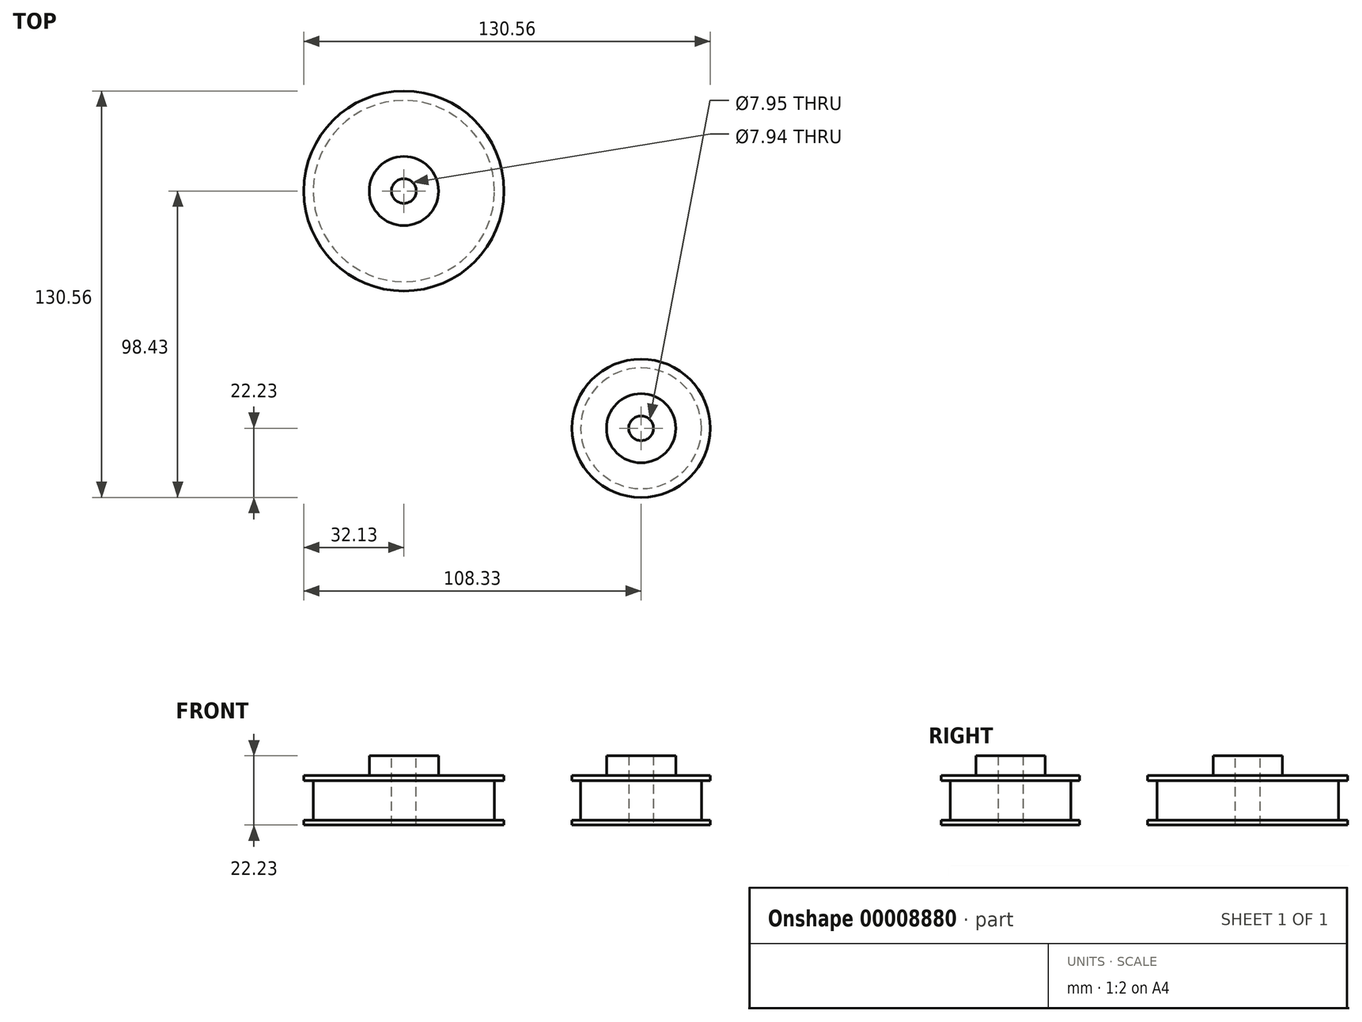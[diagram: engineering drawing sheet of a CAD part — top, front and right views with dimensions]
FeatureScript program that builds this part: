
annotation { "Feature Type Name" : "Feature", "Feature Type Description" : "" }
export const myFeature = defineFeature(function(context is Context, id is Id, definition is map)
    precondition{}
    {
        {
            var Q0;
            Q0=qCreatedBy(makeId("Front.planeOp"),FACE);
            var sketch = newSketch(context, id + "F0", { "sketchPlane" : qUnion([Q0])});
            skLineSegment(sketch, "E0", {"start": v(-11.11, 22.23) * mm, "end": v(11.11, 22.23) * mm});
            skLineSegment(sketch, "E1", {"start": v(11.11, 22.23) * mm, "end": v(11.11, 15.87) * mm});
            skLineSegment(sketch, "E2", {"start": v(11.11, 15.87) * mm, "end": v(32.13, 15.88) * mm});
            skLineSegment(sketch, "E3", {"start": v(32.13, 15.87) * mm, "end": v(32.13, 14.29) * mm});
            skLineSegment(sketch, "E4", {"start": v(32.13, 14.29) * mm, "end": v(29.1, 14.29) * mm});
            skLineSegment(sketch, "E5", {"start": v(29.1, 14.29) * mm, "end": v(29.1, 1.59) * mm});
            skLineSegment(sketch, "E6", {"start": v(29.1, 1.59) * mm, "end": v(32.13, 1.59) * mm});
            skLineSegment(sketch, "E7", {"start": v(32.13, 1.59) * mm, "end": v(32.13, 0) * mm});
            skLineSegment(sketch, "E8", {"start": v(32.13, 0) * mm, "end": v(-32.13, 0) * mm});
            skLineSegment(sketch, "E9", {"start": v(-32.13, 0) * mm, "end": v(-32.13, 1.59) * mm});
            skLineSegment(sketch, "E10", {"start": v(-32.13, 1.59) * mm, "end": v(-29.1, 1.59) * mm});
            skLineSegment(sketch, "E11", {"start": v(-29.1, 1.59) * mm, "end": v(-29.1, 14.29) * mm});
            skLineSegment(sketch, "E12", {"start": v(-29.1, 14.29) * mm, "end": v(-32.13, 14.29) * mm});
            skLineSegment(sketch, "E13", {"start": v(-32.13, 14.29) * mm, "end": v(-32.13, 15.87) * mm});
            skLineSegment(sketch, "E14", {"start": v(-32.13, 15.87) * mm, "end": v(-11.11, 15.87) * mm});
            skLineSegment(sketch, "E15", {"start": v(-11.11, 15.87) * mm, "end": v(-11.11, 22.23) * mm});
            skLineSegment(sketch, "E16", {"start": v(0, 22.23) * mm, "end": v(0, 0) * mm, "construction": true});
            skLineSegment(sketch, "E17", {"start": v(-3.97, 22.23) * mm, "end": v(-3.97, 0) * mm});
            skLineSegment(sketch, "E18", {"start": v(3.97, 22.23) * mm, "end": v(3.97, 0) * mm});
            skSolve(sketch);
        }
        {
            var Q0;
            {var subQ3=sQuery(id+"F0.wireOp",EDGE,"E1");Q0=makeQuery(id+"F0.imprint","IMPRINT",FACE,{"disambiguationData":[TD([[makeQuery(id+"F0.imprint","IMPRINT",EDGE,{"derivedFrom":subQ3}),-1.0]])]});}
            var Q1;
            Q1=sQuery(id+"F0.wireOp",EDGE,"E16");
            revolve(context, id + "F1", {"entities" : qUnion([Q0]), "axis" : qUnion([Q1]), "revolveType" : RevolveType.FULL});
        }
        {
            var Q0;
            Q0=qCreatedBy(makeId("Front.planeOp"),FACE);
            cPlane(context, id + "F2", {"entities" : qUnion([Q0]), "cplaneType" : CPlaneType.OFFSET, "offset" : 76.2 * mm, "width" : 152.4 * mm, "height" : 152.4 * mm});
        }
        {
            var Q0;
            Q0=qCreatedBy(id+"F2.planeOp",FACE);
            var sketch = newSketch(context, id + "F3", { "sketchPlane" : qUnion([Q0])});
            skLineSegment(sketch, "E19.bottom", {"start": v(65.09, 22.23) * mm, "end": v(87.31, 22.23) * mm});
            skLineSegment(sketch, "E19.left", {"start": v(65.09, 22.23) * mm, "end": v(65.09, 15.88) * mm});
            skLineSegment(sketch, "E19.right", {"start": v(87.31, 22.23) * mm, "end": v(87.31, 15.88) * mm});
            skLineSegment(sketch, "E20.bottom", {"start": v(53.98, 15.88) * mm, "end": v(65.09, 15.88) * mm});
            skLineSegment(sketch, "E20.top", {"start": v(53.98, 14.29) * mm, "end": v(56.8, 14.29) * mm});
            skLineSegment(sketch, "E20.left", {"start": v(53.97, 15.88) * mm, "end": v(53.97, 14.29) * mm});
            skLineSegment(sketch, "E20.right", {"start": v(98.42, 15.88) * mm, "end": v(98.42, 14.29) * mm});
            skLineSegment(sketch, "E21.left", {"start": v(56.8, 14.29) * mm, "end": v(56.8, 1.59) * mm});
            skLineSegment(sketch, "E21.right", {"start": v(95.6, 14.29) * mm, "end": v(95.6, 1.59) * mm});
            skLineSegment(sketch, "E22.bottom", {"start": v(53.98, 1.59) * mm, "end": v(56.8, 1.59) * mm});
            skLineSegment(sketch, "E22.top", {"start": v(53.97, 0) * mm, "end": v(98.42, 0) * mm});
            skLineSegment(sketch, "E22.left", {"start": v(53.97, 1.59) * mm, "end": v(53.97, 0) * mm});
            skLineSegment(sketch, "E22.right", {"start": v(98.42, 1.59) * mm, "end": v(98.42, 0) * mm});
            skLineSegment(sketch, "E23.trimOffspring", {"start": v(95.6, 14.29) * mm, "end": v(98.42, 14.29) * mm});
            skLineSegment(sketch, "E24.trimOffspring", {"start": v(95.6, 1.59) * mm, "end": v(98.42, 1.59) * mm});
            skLineSegment(sketch, "E25.trimOffspring", {"start": v(87.31, 15.88) * mm, "end": v(98.42, 15.88) * mm});
            skLineSegment(sketch, "E26", {"start": v(76.2, 0) * mm, "end": v(76.2, 22.23) * mm, "construction": true});
            skLineSegment(sketch, "E27", {"start": v(72.22, 22.23) * mm, "end": v(72.22, 0) * mm});
            skLineSegment(sketch, "E28", {"start": v(80.18, 0) * mm, "end": v(80.18, 22.23) * mm});
            skSolve(sketch);
        }
        {
            var Q0;
            {var subQ3=sQuery(id+"F3.wireOp",EDGE,"E19.right");Q0=makeQuery(id+"F3.imprint","IMPRINT",FACE,{"disambiguationData":[TD([[makeQuery(id+"F3.imprint","IMPRINT",EDGE,{"derivedFrom":subQ3}),-1.0]])]});}
            var Q1;
            Q1=sQuery(id+"F3.wireOp",EDGE,"E26");
            revolve(context, id + "F4", {"entities" : qUnion([Q0]), "axis" : qUnion([Q1]), "revolveType" : RevolveType.FULL});
        }
    });
